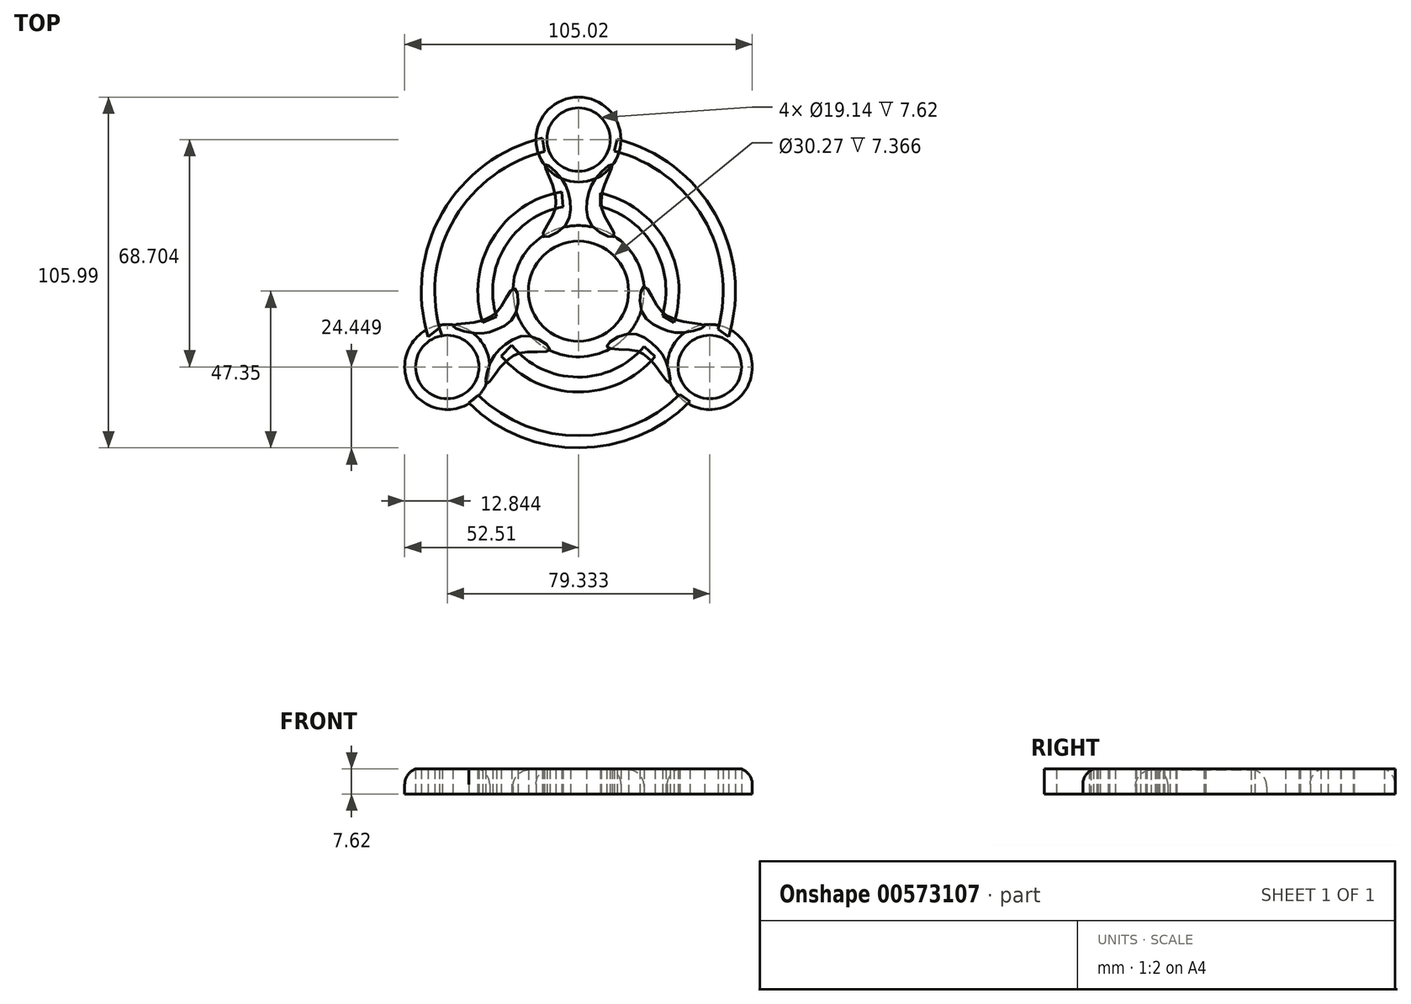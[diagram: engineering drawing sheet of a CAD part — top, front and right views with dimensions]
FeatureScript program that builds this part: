
annotation { "Feature Type Name" : "Feature", "Feature Type Description" : "" }
export const myFeature = defineFeature(function(context is Context, id is Id, definition is map)
    precondition{}
    {
        {
            var Q0;
            Q0=qCreatedBy(makeId("Top.planeOp"),FACE);
            var sketch = newSketch(context, id + "F0", { "sketchPlane" : qUnion([Q0])});
            skCircle(sketch, "E0", {"center": v(0, 0) * mm, "radius": 19.83 * mm});
            skSolve(sketch);
        }
        {
            var Q0;
            Q0=makeQuery(id+"F0.imprint","IMPRINT",FACE,{"disambiguationData":[TD([[makeQuery(id+"F0.imprint","IMPRINT",EDGE,{"derivedFrom":sQuery(id+"F0.wireOp",EDGE,"E0")}),1.0]])]});
            extrude(context, id + "F1", {"entities" : qUnion([Q0]), "depth" : 7.37 * mm, "offsetDistance" : 25.4 * mm});
        }
        {
            var Q0;
            Q0=qCreatedBy(makeId("Top.planeOp"),FACE);
            var sketch = newSketch(context, id + "F2", { "sketchPlane" : qUnion([Q0])});
            skCircle(sketch, "E1", {"center": v(0, 0) * mm, "radius": 15.13 * mm});
            skSolve(sketch);
        }
        {
            var Q0;
            Q0=makeQuery(id+"F2.imprint","IMPRINT",FACE,{"disambiguationData":[TD([[makeQuery(id+"F2.imprint","IMPRINT",EDGE,{"derivedFrom":sQuery(id+"F2.wireOp",EDGE,"E1")}),1.0]])]});
            var Q1;
            Q1=sQuery(id+"F2.wireOp",EDGE,"E1");
            extrude(context, id + "F3", {"entities" : qUnion([Q0]), "operationType" : NewBodyOperationType.REMOVE, "surfaceEntities" : qUnion([Q1]), "depth" : 8.9 * mm, "offsetDistance" : 25.4 * mm});
        }
        {
            var Q0;
            Q0=qCreatedBy(makeId("Top.planeOp"),FACE);
            var sketch = newSketch(context, id + "F4", { "sketchPlane" : qUnion([Q0])});
            skCircle(sketch, "E2", {"center": v(0, 45.8) * mm, "radius": 12.84 * mm});
            skCircle(sketch, "E3", {"center": v(0, 45.8) * mm, "radius": 9.57 * mm});
            skPoint(sketch, "E4.center", {"position": v(0, 0) * mm});
            skCircle(sketch, "E5.1.0", {"center": v(-39.67, -22.9) * mm, "radius": 9.57 * mm});
            skCircle(sketch, "E5.2.0", {"center": v(39.67, -22.9) * mm, "radius": 9.57 * mm});
            skCircle(sketch, "E6.1.0", {"center": v(-39.67, -22.9) * mm, "radius": 12.84 * mm});
            skCircle(sketch, "E6.2.0", {"center": v(39.67, -22.9) * mm, "radius": 12.84 * mm});
            skSolve(sketch);
        }
        {
            var Q0;
            Q0=makeQuery(id+"F4.imprint","IMPRINT",FACE,{"disambiguationData":[TD([[makeQuery(id+"F4.imprint","IMPRINT",EDGE,{"derivedFrom":sQuery(id+"F4.wireOp",EDGE,"oS3FJRqM-sitC-SGLY-ahM9-c0autv7Y29l7")}),1.0]])]});
            var Q1;
            Q1=makeQuery(id+"F4.imprint","IMPRINT",FACE,{"disambiguationData":[TD([[makeQuery(id+"F4.imprint","IMPRINT",EDGE,{"derivedFrom":sQuery(id+"F4.wireOp",EDGE,"E2")}),1.0]])]});
            extrude(context, id + "F5", {"entities" : qUnion([Q0, Q1]), "depth" : 7.62 * mm, "offsetDistance" : 25.4 * mm});
        }
        {
            var Q0;
            Q0=qCreatedBy(makeId("Top.planeOp"),FACE);
            var sketch = newSketch(context, id + "F6", { "sketchPlane" : qUnion([Q0])});
            skFitSpline(sketch, "E7", {"points": [v(-10.15, 38.27) * mm, v(-8.12, 32.76) * mm, v(-6.96, 28.4) * mm, v(-7.54, 23.48) * mm, v(-10.73, 16.52) * mm, v(-4.35, 19.42) * mm, v(-2.6, 27.54) * mm, v(-5.5, 34.5) * mm, v(-10.15, 38.27) * mm]});
            skFitSpline(sketch, "E8.MirrorC", {"points": [v(10.15, 38.27) * mm, v(8.12, 32.76) * mm, v(6.96, 28.4) * mm, v(7.54, 23.48) * mm, v(10.73, 16.52) * mm, v(4.35, 19.42) * mm, v(2.6, 27.54) * mm, v(5.5, 34.5) * mm, v(10.15, 38.27) * mm]});
            skFitSpline(sketch, "E9", {"points": [v(38.05, -10.45) * mm, v(32.3, -9.3) * mm, v(27.98, -8) * mm, v(24.08, -4.93) * mm, v(19.82, 1.42) * mm, v(18.96, -5.53) * mm, v(24.96, -11.26) * mm, v(32.4, -12.43) * mm, v(38.05, -10.45) * mm]});
            skFitSpline(sketch, "E10.MirrorC", {"points": [v(27.43, -27.74) * mm, v(23.8, -23.13) * mm, v(20.7, -19.86) * mm, v(16.2, -17.78) * mm, v(8.6, -16.86) * mm, v(14.4, -12.94) * mm, v(22.23, -15.7) * mm, v(26.64, -21.82) * mm, v(27.43, -27.74) * mm]});
            skFitSpline(sketch, "E11", {"points": [v(-27.83, -28.06) * mm, v(-24.07, -23.56) * mm, v(-20.88, -20.38) * mm, v(-16.32, -18.42) * mm, v(-8.7, -17.72) * mm, v(-14.4, -13.64) * mm, v(-22.3, -16.18) * mm, v(-26.88, -22.16) * mm, v(-27.83, -28.06) * mm]});
            skFitSpline(sketch, "E12.MirrorC", {"points": [v(-37.95, -10.48) * mm, v(-32.17, -9.49) * mm, v(-27.82, -8.32) * mm, v(-23.84, -5.36) * mm, v(-19.4, 0.87) * mm, v(-18.73, -6.1) * mm, v(-24.9, -11.66) * mm, v(-32.37, -12.62) * mm, v(-37.95, -10.48) * mm]});
            skSolve(sketch);
        }
        {
            var Q0;
            Q0 = qSketchRegion(id + "F6", true);
            extrude(context, id + "F7", {"entities" : qUnion([Q0]), "depth" : 7.62 * mm, "offsetDistance" : 25.4 * mm});
        }
        {
            var Q0;
            Q0 = qSketchRegion(id + "F4", true);
            extrude(context, id + "F8", {"entities" : qUnion([Q0]), "depth" : 7.62 * mm, "offsetDistance" : 25.4 * mm});
        }
        {
            var Q0;
            Q0=qCreatedBy(makeId("Top.planeOp"),FACE);
            var sketch = newSketch(context, id + "F9", { "sketchPlane" : qUnion([Q0])});
            skArc(sketch, "E13", {"start": v(-5.07, 30) * mm, "mid": v(-26.04, 15.74) * mm, "end": v(-28.93, -9.45) * mm});
            skArc(sketch, "E14", {"start": v(-23.34, -19.57) * mm, "mid": v(-0.16, -30.45) * mm, "end": v(23.13, -19.8) * mm});
            skArc(sketch, "E15", {"start": v(28.84, -9.42) * mm, "mid": v(26.36, 15.04) * mm, "end": v(6.57, 29.62) * mm});
            skArc(sketch, "E16", {"start": v(-20.15, -16.38) * mm, "mid": v(-0.25, -25.96) * mm, "end": v(19.83, -16.76) * mm});
            skArc(sketch, "E17", {"start": v(25.37, -7.4) * mm, "mid": v(22.95, 13.08) * mm, "end": v(6.57, 25.6) * mm});
            skArc(sketch, "E18", {"start": v(-24.79, -7.68) * mm, "mid": v(-22.2, 13.43) * mm, "end": v(-4.7, 25.52) * mm});
            skLineSegment(sketch, "E19", {"start": v(-5.07, 30) * mm, "end": v(-4.7, 25.52) * mm});
            skLineSegment(sketch, "E20", {"start": v(-24.79, -7.68) * mm, "end": v(-28.93, -9.45) * mm});
            skLineSegment(sketch, "E21", {"start": v(25.37, -7.4) * mm, "end": v(28.84, -9.42) * mm});
            skLineSegment(sketch, "E22", {"start": v(6.57, 29.62) * mm, "end": v(6.57, 25.6) * mm});
            skLineSegment(sketch, "E23", {"start": v(19.83, -16.76) * mm, "end": v(23.13, -19.8) * mm});
            skLineSegment(sketch, "E24", {"start": v(-20.15, -16.38) * mm, "end": v(-23.34, -19.57) * mm});
            skSolve(sketch);
        }
        {
            var Q0;
            Q0 = qSketchRegion(id + "F9", true);
            extrude(context, id + "F10", {"entities" : qUnion([Q0]), "depth" : 7.62 * mm, "offsetDistance" : 25.4 * mm});
        }
        {
            var Q0;
            Q0=qCreatedBy(makeId("Top.planeOp"),FACE);
            var sketch = newSketch(context, id + "F11", { "sketchPlane" : qUnion([Q0])});
            skArc(sketch, "E25", {"start": v(-10.87, 46.24) * mm, "mid": v(-41.16, 23.7) * mm, "end": v(-45.45, -13.8) * mm});
            skArc(sketch, "E26", {"start": v(-33.2, -33.77) * mm, "mid": v(0.3, -47.35) * mm, "end": v(33.63, -33.34) * mm});
            skArc(sketch, "E27", {"start": v(45.37, -13.8) * mm, "mid": v(41.3, 23.3) * mm, "end": v(11.67, 45.96) * mm});
            skArc(sketch, "E28", {"start": v(-10.3, 42.18) * mm, "mid": v(-38.02, 20.97) * mm, "end": v(-41.17, -13.8) * mm});
            skArc(sketch, "E29", {"start": v(-30.3, -31.45) * mm, "mid": v(0.2, -43.67) * mm, "end": v(30.6, -31.16) * mm});
            skArc(sketch, "E30", {"start": v(42.18, -11.45) * mm, "mid": v(37.76, 22) * mm, "end": v(10.83, 42.34) * mm});
            skLineSegment(sketch, "E31", {"start": v(-45.45, -13.8) * mm, "end": v(-41.97, -11.1) * mm});
            skLineSegment(sketch, "E32", {"start": v(-41.97, -11.1) * mm, "end": v(-41.17, -13.8) * mm});
            skLineSegment(sketch, "E33", {"start": v(-10.87, 46.24) * mm, "end": v(-10.3, 42.18) * mm});
            skLineSegment(sketch, "E34", {"start": v(11.67, 45.96) * mm, "end": v(10.83, 42.34) * mm});
            skLineSegment(sketch, "E35", {"start": v(42.18, -11.45) * mm, "end": v(45.37, -13.8) * mm});
            skLineSegment(sketch, "E36", {"start": v(30.6, -31.16) * mm, "end": v(33.63, -33.34) * mm});
            skLineSegment(sketch, "E37", {"start": v(-30.3, -31.45) * mm, "end": v(-33.2, -33.77) * mm});
            skSolve(sketch);
        }
        {
            var Q0;
            Q0 = qSketchRegion(id + "F11", true);
            extrude(context, id + "F12", {"entities" : qUnion([Q0]), "depth" : 7.62 * mm, "offsetDistance" : 25.4 * mm});
        }
        {
            var Q0;
            Q0=makeQuery(id+"F8.opExtrude","CAP_EDGE",EDGE,{"disambiguationData":[OSD([sQuery(id+"F4.wireOp",EDGE,"E6.1.0")])],"isStart":false});
            var Q1;
            Q1=makeQuery(id+"F12.opExtrude","CAP_EDGE",EDGE,{"disambiguationData":[OSD([sQuery(id+"F11.wireOp",EDGE,"E25")])],"isStart":false});
            var Q2;
            {var subQ0=sQuery(id+"F11.wireOp",EDGE,"E28");Q2=makeQuery(id+"F12.opExtrude","CAP_EDGE",EDGE,{"disambiguationData":[OSD([subQ0]),TDD([makeQuery(id+"F11.imprint","IMPRINT",EDGE,{"disambiguationData":[TD([[makeQuery(id+"F11.imprint","INTERSECT",VERTEX,{"derivedFrom":[subQ0,sQuery(id+"F11.wireOp",EDGE,"E33")]}),-1.0]])],"derivedFrom":subQ0})])],"isStart":false});}
            var Q3;
            Q3=makeQuery(id+"F10.opExtrude","CAP_EDGE",EDGE,{"disambiguationData":[OSD([sQuery(id+"F9.wireOp",EDGE,"E13")])],"isStart":false});
            var Q4;
            Q4=makeQuery(id+"F10.opExtrude","CAP_EDGE",EDGE,{"disambiguationData":[OSD([sQuery(id+"F9.wireOp",EDGE,"E18")])],"isStart":false});
            var Q5;
            Q5=makeQuery(id+"F7.opExtrude","CAP_EDGE",EDGE,{"disambiguationData":[OSD([sQuery(id+"F6.wireOp",EDGE,"E12.MirrorC")])],"isStart":false});
            var Q6;
            Q6=makeQuery(id+"F7.opExtrude","CAP_EDGE",EDGE,{"disambiguationData":[OSD([sQuery(id+"F6.wireOp",EDGE,"E11")])],"isStart":false});
            var Q7;
            Q7=makeQuery(id+"F10.opExtrude","CAP_EDGE",EDGE,{"disambiguationData":[OSD([sQuery(id+"F9.wireOp",EDGE,"E16")])],"isStart":false});
            var Q8;
            Q8=makeQuery(id+"F10.opExtrude","CAP_EDGE",EDGE,{"disambiguationData":[OSD([sQuery(id+"F9.wireOp",EDGE,"E14")])],"isStart":false});
            var Q9;
            Q9=makeQuery(id+"F12.opExtrude","CAP_EDGE",EDGE,{"disambiguationData":[OSD([sQuery(id+"F11.wireOp",EDGE,"E29")])],"isStart":false});
            var Q10;
            Q10=makeQuery(id+"F12.opExtrude","CAP_EDGE",EDGE,{"disambiguationData":[OSD([sQuery(id+"F11.wireOp",EDGE,"E26")])],"isStart":false});
            var Q11;
            Q11=makeQuery(id+"F8.opExtrude","CAP_EDGE",EDGE,{"disambiguationData":[OSD([sQuery(id+"F4.wireOp",EDGE,"E6.2.0")])],"isStart":false});
            var Q12;
            Q12=makeQuery(id+"F7.opExtrude","CAP_EDGE",EDGE,{"disambiguationData":[OSD([sQuery(id+"F6.wireOp",EDGE,"E10.MirrorC")])],"isStart":false});
            var Q13;
            Q13=makeQuery(id+"F7.opExtrude","CAP_EDGE",EDGE,{"disambiguationData":[OSD([sQuery(id+"F6.wireOp",EDGE,"E9")])],"isStart":false});
            var Q14;
            Q14=makeQuery(id+"F1.opExtrude","CAP_EDGE",EDGE,{"disambiguationData":[OSD([sQuery(id+"F0.wireOp",EDGE,"E0")])],"isStart":false});
            var Q15;
            Q15=makeQuery(id+"F7.opExtrude","CAP_EDGE",EDGE,{"disambiguationData":[OSD([sQuery(id+"F6.wireOp",EDGE,"E8.MirrorC")])],"isStart":false});
            var Q16;
            Q16=makeQuery(id+"F7.opExtrude","CAP_EDGE",EDGE,{"disambiguationData":[OSD([sQuery(id+"F6.wireOp",EDGE,"E7")])],"isStart":false});
            var Q17;
            Q17=makeQuery(id+"F5.opExtrude","CAP_EDGE",EDGE,{"disambiguationData":[OSD([sQuery(id+"F4.wireOp",EDGE,"E2")])],"isStart":false});
            var Q18;
            Q18=makeQuery(id+"F10.opExtrude","CAP_EDGE",EDGE,{"disambiguationData":[OSD([sQuery(id+"F9.wireOp",EDGE,"E15")])],"isStart":false});
            var Q19;
            Q19=makeQuery(id+"F10.opExtrude","CAP_EDGE",EDGE,{"disambiguationData":[OSD([sQuery(id+"F9.wireOp",EDGE,"E17")])],"isStart":false});
            var Q20;
            Q20=makeQuery(id+"F12.opExtrude","CAP_EDGE",EDGE,{"disambiguationData":[OSD([sQuery(id+"F11.wireOp",EDGE,"E30")])],"isStart":false});
            var Q21;
            Q21=makeQuery(id+"F12.opExtrude","CAP_EDGE",EDGE,{"disambiguationData":[OSD([sQuery(id+"F11.wireOp",EDGE,"E27")])],"isStart":false});
            fillet(context, id + "F13", {"entities" : qUnion([Q0, Q1, Q2, Q3, Q4, Q5, Q6, Q7, Q8, Q9, Q10, Q11, Q12, Q13, Q14, Q15, Q16, Q17, Q18, Q19, Q20, Q21]), "radius" : 5.08 * mm, "tangentPropagation" : true, "allowEdgeOverflow" : false});
        }
    });
